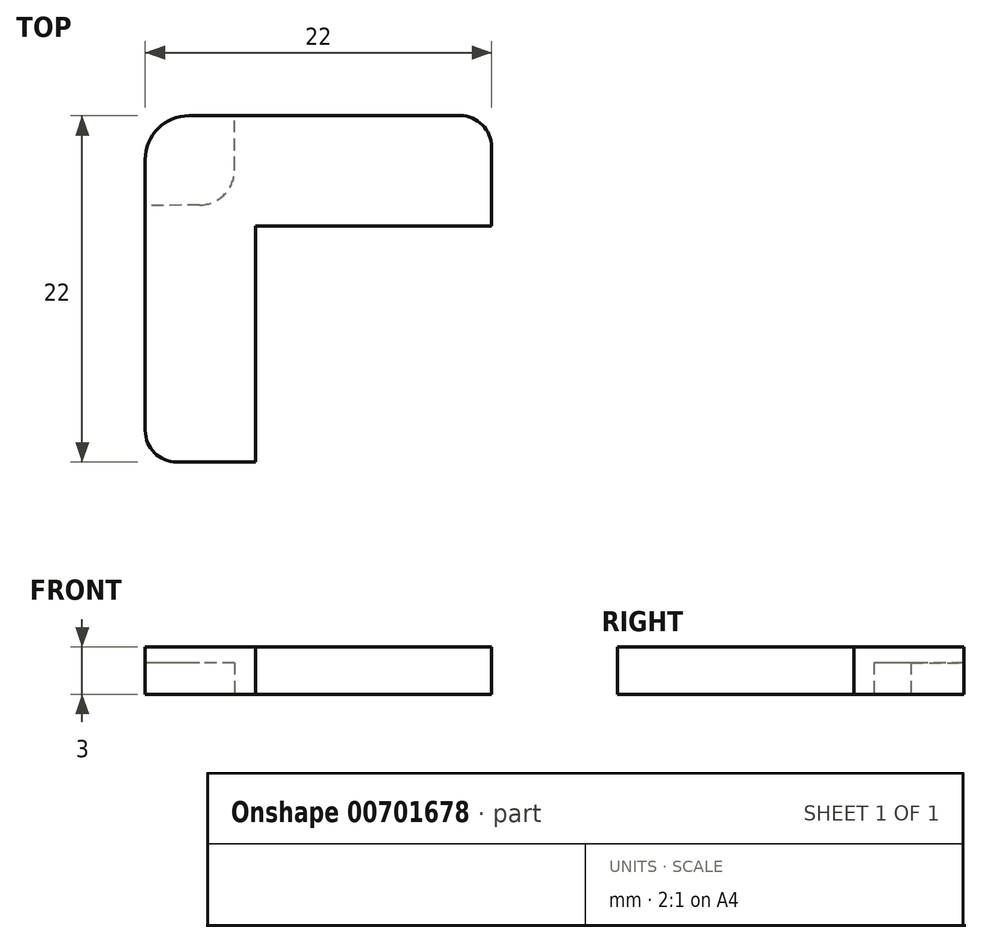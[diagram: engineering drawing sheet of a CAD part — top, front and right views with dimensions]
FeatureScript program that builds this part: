
annotation { "Feature Type Name" : "Feature", "Feature Type Description" : "" }
export const myFeature = defineFeature(function(context is Context, id is Id, definition is map)
    precondition{}
    {
        {
            var Q0;
            Q0=qCreatedBy(makeId("Top.planeOp"),FACE);
            var sketch = newSketch(context, id + "F0", { "sketchPlane" : qUnion([Q0])});
            skLineSegment(sketch, "E0", {"start": v(0, 0) * mm, "end": v(15, 0) * mm});
            skLineSegment(sketch, "E1", {"start": v(0, 0) * mm, "end": v(0, -15) * mm});
            skLineSegment(sketch, "E2", {"start": v(0, -15) * mm, "end": v(-7, -15) * mm});
            skLineSegment(sketch, "E3", {"start": v(15, 0) * mm, "end": v(15, 7) * mm});
            skLineSegment(sketch, "E4", {"start": v(15, 7) * mm, "end": v(-7, 7) * mm});
            skLineSegment(sketch, "E5", {"start": v(-7, 7) * mm, "end": v(-7, -15) * mm});
            skSolve(sketch);
        }
        {
            var Q0;
            Q0=makeQuery(id+"F0.imprint","IMPRINT",FACE,{"disambiguationData":[TD([[makeQuery(id+"F0.imprint","IMPRINT",EDGE,{"derivedFrom":sQuery(id+"F0.wireOp",EDGE,"E0")}),1.0]])]});
            extrude(context, id + "F1", {"entities" : qUnion([Q0]), "depth" : 3 * mm, "offsetDistance" : 25 * mm});
        }
        {
            var Q0;
            Q0=makeQuery(id+"F1.opExtrude","SWEPT_EDGE",EDGE,{"disambiguationData":[OSD([sQuery(id+"F0.wireOp",EDGE,"E4"),sQuery(id+"F0.wireOp",EDGE,"E5")])]});
            fillet(context, id + "F2", {"entities" : qUnion([Q0]), "radius" : 2.8 * mm, "tangentPropagation" : true, "allowEdgeOverflow" : false});
        }
        {
            var Q0;
            Q0=makeQuery(id+"F1.opExtrude","SWEPT_EDGE",EDGE,{"disambiguationData":[OSD([sQuery(id+"F0.wireOp",EDGE,"E3"),sQuery(id+"F0.wireOp",EDGE,"E4")])]});
            var Q1;
            Q1=makeQuery(id+"F1.opExtrude","SWEPT_EDGE",EDGE,{"disambiguationData":[OSD([sQuery(id+"F0.wireOp",EDGE,"E2"),sQuery(id+"F0.wireOp",EDGE,"E5")])]});
            fillet(context, id + "F3", {"entities" : qUnion([Q0, Q1]), "radius" : 2 * mm, "tangentPropagation" : true, "allowEdgeOverflow" : false});
        }
        {
            var Q0;
            Q0=makeQuery(id+"F1.opExtrude","CAP_FACE",FACE,{"disambiguationData":[OSD([sQuery(id+"F0.wireOp",EDGE,"E0"),sQuery(id+"F0.wireOp",EDGE,"E1"),sQuery(id+"F0.wireOp",EDGE,"E2"),sQuery(id+"F0.wireOp",EDGE,"E3"),sQuery(id+"F0.wireOp",EDGE,"E4"),sQuery(id+"F0.wireOp",EDGE,"E5")])],"isStart":true});
            var sketch = newSketch(context, id + "F4", { "sketchPlane" : qUnion([Q0])});
            skCircle(sketch, "E6", {"center": v(-3.57, -3.57) * mm, "radius": 2.25 * mm});
            skLineSegment(sketch, "E7", {"start": v(-1.32, -3.64) * mm, "end": v(-1.32, -7) * mm});
            skLineSegment(sketch, "E8", {"start": v(-3.55, -1.32) * mm, "end": v(-7, -1.28) * mm});
            skSolve(sketch);
        }
        {
            var Q0;
            Q0=makeQuery(id+"F4.imprint","IMPRINT",FACE,{"disambiguationData":[TD([[makeQuery(id+"F4.imprint","IMPRINT",EDGE,{"derivedFrom":sQuery(id+"F4.wireOp",EDGE,"E6")}),1.0]])]});
            var Q1;
            {var subQ4=sQuery(id+"F4.wireOp",EDGE,"E7");Q1=makeQuery(id+"F4.imprint","IMPRINT",FACE,{"disambiguationData":[TD([[makeQuery(id+"F4.imprint","IMPRINT",EDGE,{"derivedFrom":subQ4}),-1.0]])]});}
            extrude(context, id + "F5", {"entities" : qUnion([Q0, Q1]), "operationType" : NewBodyOperationType.REMOVE, "oppositeDirection" : true, "depth" : 2 * mm, "offsetDistance" : 25 * mm});
        }
    });
